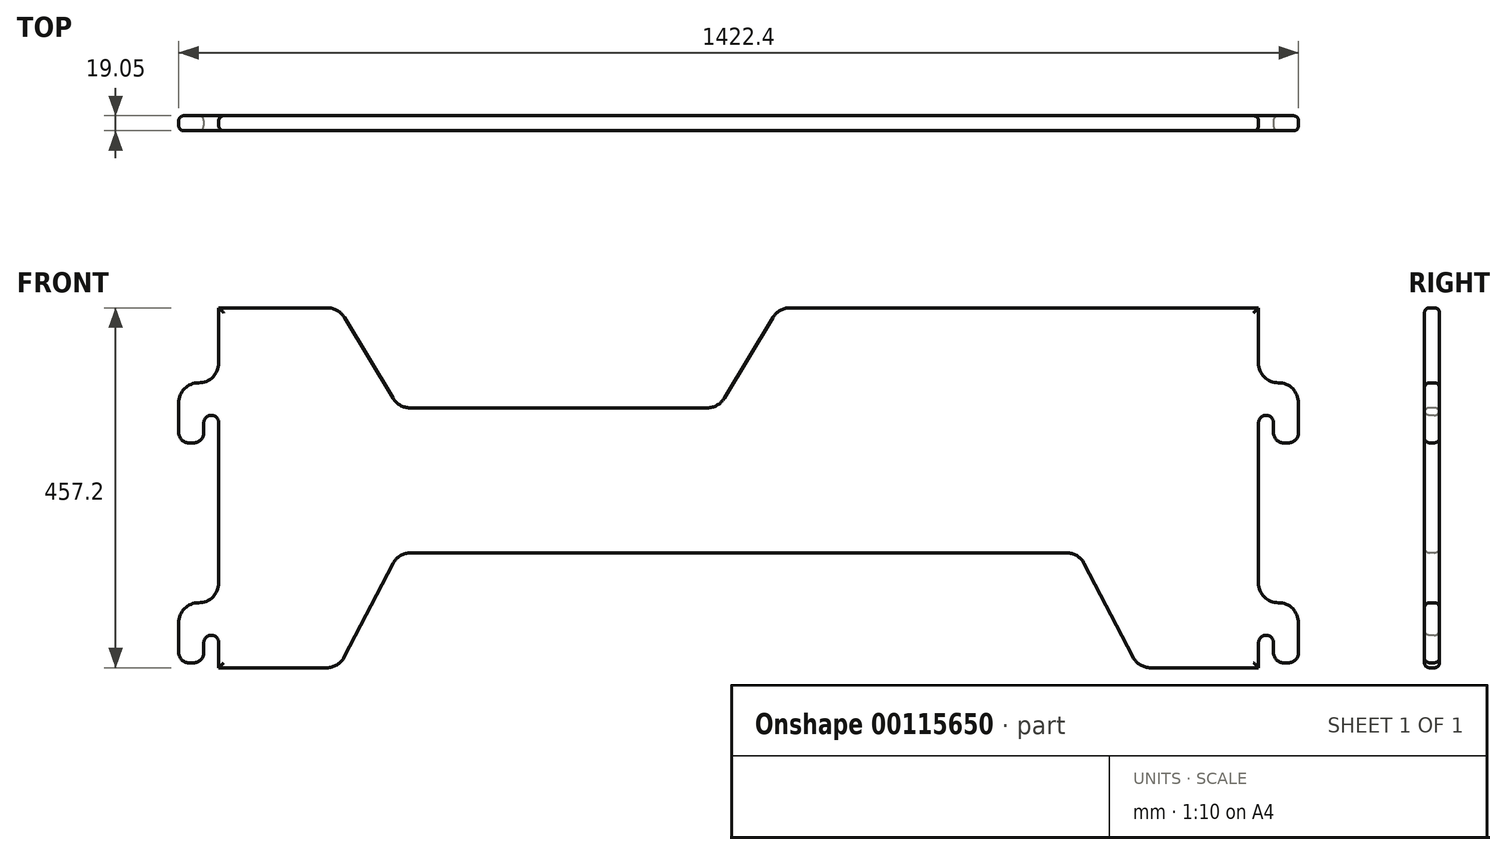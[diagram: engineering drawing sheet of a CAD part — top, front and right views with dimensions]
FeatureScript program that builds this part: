
annotation { "Feature Type Name" : "Feature", "Feature Type Description" : "" }
export const myFeature = defineFeature(function(context is Context, id is Id, definition is map)
    precondition{}
    {
        {
            var Q0;
            Q0=qCreatedBy(makeId("Front.planeOp"),FACE);
            var sketch = newSketch(context, id + "F0", { "sketchPlane" : qUnion([Q0])});
            skLineSegment(sketch, "E0.bottom", {"start": v(-660.4, 457.2) * mm, "end": v(-508, 457.2) * mm});
            skLineSegment(sketch, "E0.top", {"start": v(-660.4, 0) * mm, "end": v(-508, 0) * mm});
            skLineSegment(sketch, "E0.left", {"start": v(-660.4, 457.2) * mm, "end": v(-660.4, 0) * mm});
            skLineSegment(sketch, "E0.right", {"start": v(660.4, 457.2) * mm, "end": v(660.4, 0) * mm});
            skLineSegment(sketch, "E1", {"start": v(-508, 0) * mm, "end": v(-431.8, 146.05) * mm});
            skLineSegment(sketch, "E2", {"start": v(-431.8, 146.05) * mm, "end": v(431.8, 146.05) * mm});
            skLineSegment(sketch, "E3", {"start": v(431.8, 146.05) * mm, "end": v(508, 0) * mm});
            skLineSegment(sketch, "E4.trimOffspring", {"start": v(508, 0) * mm, "end": v(660.4, 0) * mm});
            skLineSegment(sketch, "E5", {"start": v(0, 457.2) * mm, "end": v(0, 0) * mm, "construction": true});
            skLineSegment(sketch, "E6", {"start": v(-508, 457.2) * mm, "end": v(-431.8, 330.2) * mm});
            skLineSegment(sketch, "E7", {"start": v(-431.8, 330.2) * mm, "end": v(-25.4, 330.2) * mm});
            skLineSegment(sketch, "E8", {"start": v(-25.4, 330.2) * mm, "end": v(50.8, 457.2) * mm});
            skLineSegment(sketch, "E9.trimOffspring", {"start": v(50.8, 457.2) * mm, "end": v(660.4, 457.2) * mm});
            skLineSegment(sketch, "E10", {"start": v(-660.4, 203.2) * mm, "end": v(660.4, 203.2) * mm, "construction": true});
            skLineSegment(sketch, "E11", {"start": v(660.4, 355.6) * mm, "end": v(-660.4, 355.6) * mm, "construction": true});
            skLineSegment(sketch, "E12", {"start": v(660.4, 361.95) * mm, "end": v(685.8, 361.95) * mm});
            skLineSegment(sketch, "E13", {"start": v(711.2, 336.55) * mm, "end": v(711.2, 298.45) * mm});
            skLineSegment(sketch, "E14", {"start": v(698.5, 285.75) * mm, "end": v(692.15, 285.75) * mm});
            skLineSegment(sketch, "E15", {"start": v(679.45, 298.45) * mm, "end": v(679.45, 311.15) * mm});
            skArc(sketch, "E16", {"start": v(679.45, 311.15) * mm, "mid": v(669.93, 320.68) * mm, "end": v(660.4, 311.15) * mm});
            skArc(sketch, "E17", {"start": v(679.45, 31.75) * mm, "mid": v(669.93, 41.28) * mm, "end": v(660.4, 31.75) * mm});
            skLineSegment(sketch, "E18", {"start": v(679.45, 31.75) * mm, "end": v(679.45, 19.05) * mm});
            skLineSegment(sketch, "E19", {"start": v(692.15, 6.35) * mm, "end": v(698.5, 6.35) * mm});
            skLineSegment(sketch, "E20", {"start": v(711.2, 19.05) * mm, "end": v(711.2, 57.15) * mm});
            skLineSegment(sketch, "E21", {"start": v(685.8, 82.55) * mm, "end": v(660.4, 82.55) * mm});
            skPoint(sketch, "E22.visualSharp", {"position": v(711.2, 82.55) * mm});
            skArc(sketch, "E22.filletArc", {"start": v(711.2, 57.15) * mm, "mid": v(703.76, 75.11) * mm, "end": v(685.8, 82.55) * mm});
            skPoint(sketch, "E23.visualSharp", {"position": v(711.2, 361.95) * mm});
            skArc(sketch, "E23.filletArc", {"start": v(711.2, 336.55) * mm, "mid": v(703.76, 354.51) * mm, "end": v(685.8, 361.95) * mm});
            skPoint(sketch, "E24.visualSharp", {"position": v(679.45, 285.75) * mm});
            skArc(sketch, "E24.filletArc", {"start": v(679.45, 298.45) * mm, "mid": v(683.17, 289.47) * mm, "end": v(692.15, 285.75) * mm});
            skPoint(sketch, "E25.visualSharp", {"position": v(711.2, 285.75) * mm});
            skArc(sketch, "E25.filletArc", {"start": v(698.5, 285.75) * mm, "mid": v(707.48, 289.47) * mm, "end": v(711.2, 298.45) * mm});
            skPoint(sketch, "E26.visualSharp", {"position": v(679.45, 6.35) * mm});
            skArc(sketch, "E26.filletArc", {"start": v(679.45, 19.05) * mm, "mid": v(683.17, 10.07) * mm, "end": v(692.15, 6.35) * mm});
            skPoint(sketch, "E27.visualSharp", {"position": v(711.2, 6.35) * mm});
            skArc(sketch, "E27.filletArc", {"start": v(698.5, 6.35) * mm, "mid": v(707.48, 10.07) * mm, "end": v(711.2, 19.05) * mm});
            skArc(sketch, "E28.MirrorCS", {"start": v(-698.5, 285.75) * mm, "mid": v(-707.48, 289.47) * mm, "end": v(-711.2, 298.45) * mm});
            skLineSegment(sketch, "E29.MirrorCS", {"start": v(-698.5, 285.75) * mm, "end": v(-692.15, 285.75) * mm});
            skLineSegment(sketch, "E30.MirrorCS", {"start": v(-679.45, 298.45) * mm, "end": v(-679.45, 311.15) * mm});
            skLineSegment(sketch, "E31.MirrorCS", {"start": v(-692.15, 6.35) * mm, "end": v(-698.5, 6.35) * mm});
            skArc(sketch, "E32.MirrorCS", {"start": v(-679.45, 311.15) * mm, "mid": v(-669.93, 320.68) * mm, "end": v(-660.4, 311.15) * mm});
            skArc(sketch, "E33.MirrorCS", {"start": v(-679.45, 298.45) * mm, "mid": v(-683.17, 289.47) * mm, "end": v(-692.15, 285.75) * mm});
            skArc(sketch, "E34.MirrorCS", {"start": v(-679.45, 19.05) * mm, "mid": v(-683.17, 10.07) * mm, "end": v(-692.15, 6.35) * mm});
            skArc(sketch, "E35.MirrorCS", {"start": v(-679.45, 31.75) * mm, "mid": v(-669.93, 41.27) * mm, "end": v(-660.4, 31.75) * mm});
            skArc(sketch, "E36.MirrorCS", {"start": v(-698.5, 6.35) * mm, "mid": v(-707.48, 10.07) * mm, "end": v(-711.2, 19.05) * mm});
            skLineSegment(sketch, "E37.MirrorCS", {"start": v(-679.45, 31.75) * mm, "end": v(-679.45, 19.05) * mm});
            skLineSegment(sketch, "E38.MirrorCS", {"start": v(-711.2, 336.55) * mm, "end": v(-711.2, 298.45) * mm});
            skArc(sketch, "E39.MirrorCS", {"start": v(-711.2, 336.55) * mm, "mid": v(-703.76, 354.51) * mm, "end": v(-685.8, 361.95) * mm});
            skArc(sketch, "E40.MirrorCS", {"start": v(-711.2, 57.15) * mm, "mid": v(-703.76, 75.11) * mm, "end": v(-685.8, 82.55) * mm});
            skLineSegment(sketch, "E41.MirrorCS", {"start": v(-711.2, 19.05) * mm, "end": v(-711.2, 57.15) * mm});
            skLineSegment(sketch, "E42.MirrorCS", {"start": v(-685.8, 82.55) * mm, "end": v(-660.4, 82.55) * mm});
            skLineSegment(sketch, "E43.MirrorCS", {"start": v(-660.4, 361.95) * mm, "end": v(-685.8, 361.95) * mm});
            skPoint(sketch, "E44.MirrorP", {"position": v(-711.2, 6.35) * mm});
            skPoint(sketch, "E45.MirrorP", {"position": v(-711.2, 82.55) * mm});
            skPoint(sketch, "E46.MirrorP", {"position": v(-711.2, 361.95) * mm});
            skPoint(sketch, "E47.MirrorP", {"position": v(-711.2, 285.75) * mm});
            skPoint(sketch, "E48.MirrorP", {"position": v(-679.45, 6.35) * mm});
            skPoint(sketch, "E49.MirrorP", {"position": v(-679.45, 285.75) * mm});
            skSolve(sketch);
        }
        {
            var Q0;
            Q0 = qSketchRegion(id + "F0", true);
            extrude(context, id + "F1", {"entities" : qUnion([Q0]), "oppositeDirection" : true, "depth" : 19.05 * mm});
        }
        {
            var Q0;
            Q0=makeQuery(id+"F1.opExtrude","SWEPT_EDGE",EDGE,{"disambiguationData":[OSD([sQuery(id+"F0.wireOp",EDGE,"E0.bottom"),sQuery(id+"F0.wireOp",EDGE,"E6")])]});
            var Q1;
            Q1=makeQuery(id+"F1.opExtrude","SWEPT_EDGE",EDGE,{"disambiguationData":[OSD([sQuery(id+"F0.wireOp",EDGE,"E6"),sQuery(id+"F0.wireOp",EDGE,"E7")])]});
            var Q2;
            Q2=makeQuery(id+"F1.opExtrude","SWEPT_EDGE",EDGE,{"disambiguationData":[OSD([sQuery(id+"F0.wireOp",EDGE,"E8"),sQuery(id+"F0.wireOp",EDGE,"E9.trimOffspring")])]});
            var Q3;
            Q3=makeQuery(id+"F1.opExtrude","SWEPT_EDGE",EDGE,{"disambiguationData":[OSD([sQuery(id+"F0.wireOp",EDGE,"E7"),sQuery(id+"F0.wireOp",EDGE,"E8")])]});
            var Q4;
            Q4=makeQuery(id+"F1.opExtrude","SWEPT_EDGE",EDGE,{"disambiguationData":[OSD([sQuery(id+"F0.wireOp",EDGE,"E2"),sQuery(id+"F0.wireOp",EDGE,"E3")])]});
            var Q5;
            Q5=makeQuery(id+"F1.opExtrude","SWEPT_EDGE",EDGE,{"disambiguationData":[OSD([sQuery(id+"F0.wireOp",EDGE,"E3"),sQuery(id+"F0.wireOp",EDGE,"E4.trimOffspring")])]});
            var Q6;
            Q6=makeQuery(id+"F1.opExtrude","SWEPT_EDGE",EDGE,{"disambiguationData":[OSD([sQuery(id+"F0.wireOp",EDGE,"E1"),sQuery(id+"F0.wireOp",EDGE,"E2")])]});
            var Q7;
            Q7=makeQuery(id+"F1.opExtrude","SWEPT_EDGE",EDGE,{"disambiguationData":[OSD([sQuery(id+"F0.wireOp",EDGE,"E0.top"),sQuery(id+"F0.wireOp",EDGE,"E1")])]});
            var Q8;
            Q8=makeQuery(id+"F1.opExtrude","SWEPT_EDGE",EDGE,{"disambiguationData":[OSD([sQuery(id+"F0.wireOp",EDGE,"E0.right"),sQuery(id+"F0.wireOp",EDGE,"E12")])]});
            var Q9;
            Q9=makeQuery(id+"F1.opExtrude","SWEPT_EDGE",EDGE,{"disambiguationData":[OSD([sQuery(id+"F0.wireOp",EDGE,"E0.right"),sQuery(id+"F0.wireOp",EDGE,"E21")])]});
            var Q10;
            Q10=makeQuery(id+"F1.opExtrude","SWEPT_EDGE",EDGE,{"disambiguationData":[OSD([sQuery(id+"F0.wireOp",EDGE,"E0.left"),sQuery(id+"F0.wireOp",EDGE,"E42.MirrorCS")])]});
            var Q11;
            Q11=makeQuery(id+"F1.opExtrude","SWEPT_EDGE",EDGE,{"disambiguationData":[OSD([sQuery(id+"F0.wireOp",EDGE,"E0.left"),sQuery(id+"F0.wireOp",EDGE,"E43.MirrorCS")])]});
            fillet(context, id + "F2", {"entities" : qUnion([Q0, Q1, Q2, Q3, Q4, Q5, Q6, Q7, Q8, Q9, Q10, Q11]), "radius" : 25.4 * mm, "tangentPropagation" : true, "allowEdgeOverflow" : false});
        }
        {
            var Q0;
            Q0=makeQuery(id+"F1.opExtrude","CAP_EDGE",EDGE,{"disambiguationData":[OSD([sQuery(id+"F0.wireOp",EDGE,"E7")])],"isStart":true});
            var Q1;
            Q1=makeQuery(id+"F1.opExtrude","CAP_EDGE",EDGE,{"disambiguationData":[OSD([sQuery(id+"F0.wireOp",EDGE,"E2")])],"isStart":true});
            var Q2;
            Q2=makeQuery(id+"F1.opExtrude","CAP_EDGE",EDGE,{"disambiguationData":[OSD([sQuery(id+"F0.wireOp",EDGE,"E7")])],"isStart":false});
            var Q3;
            Q3=makeQuery(id+"F1.opExtrude","CAP_EDGE",EDGE,{"disambiguationData":[OSD([sQuery(id+"F0.wireOp",EDGE,"E2")])],"isStart":false});
            var Q4;
            {var subQ0=sQuery(id+"F0.wireOp",EDGE,"E0.left");Q4=makeQuery(id+"F1.opExtrude","CAP_EDGE",EDGE,{"disambiguationData":[OSD([subQ0]),TDD([makeQuery(id+"F0.imprint","IMPRINT",EDGE,{"disambiguationData":[TD([[makeQuery(id+"F0.imprint","INTERSECT",VERTEX,{"derivedFrom":[subQ0,sQuery(id+"F0.wireOp",EDGE,"E32.MirrorCS")]}),-1.0]])],"derivedFrom":subQ0})])],"isStart":false});}
            var Q5;
            {var subQ0=sQuery(id+"F0.wireOp",EDGE,"E0.left");Q5=makeQuery(id+"F1.opExtrude","CAP_EDGE",EDGE,{"disambiguationData":[OSD([subQ0]),TDD([makeQuery(id+"F0.imprint","IMPRINT",EDGE,{"disambiguationData":[TD([[makeQuery(id+"F0.imprint","INTERSECT",VERTEX,{"derivedFrom":[subQ0,sQuery(id+"F0.wireOp",EDGE,"E32.MirrorCS")]}),-1.0]])],"derivedFrom":subQ0})])],"isStart":true});}
            var Q6;
            {var subQ0=sQuery(id+"F0.wireOp",EDGE,"E0.right");Q6=makeQuery(id+"F1.opExtrude","CAP_EDGE",EDGE,{"disambiguationData":[OSD([subQ0]),TDD([makeQuery(id+"F0.imprint","IMPRINT",EDGE,{"disambiguationData":[TD([[makeQuery(id+"F0.imprint","INTERSECT",VERTEX,{"derivedFrom":[subQ0,sQuery(id+"F0.wireOp",EDGE,"E16")]}),-1.0]])],"derivedFrom":subQ0})])],"isStart":true});}
            var Q7;
            {var subQ0=sQuery(id+"F0.wireOp",EDGE,"E0.right");Q7=makeQuery(id+"F1.opExtrude","CAP_EDGE",EDGE,{"disambiguationData":[OSD([subQ0]),TDD([makeQuery(id+"F0.imprint","IMPRINT",EDGE,{"disambiguationData":[TD([[makeQuery(id+"F0.imprint","INTERSECT",VERTEX,{"derivedFrom":[subQ0,sQuery(id+"F0.wireOp",EDGE,"E16")]}),-1.0]])],"derivedFrom":subQ0})])],"isStart":false});}
            fillet(context, id + "F3", {"entities" : qUnion([Q0, Q1, Q2, Q3, Q4, Q5, Q6, Q7]), "radius" : 6.35 * mm, "tangentPropagation" : true, "allowEdgeOverflow" : false});
        }
    });
